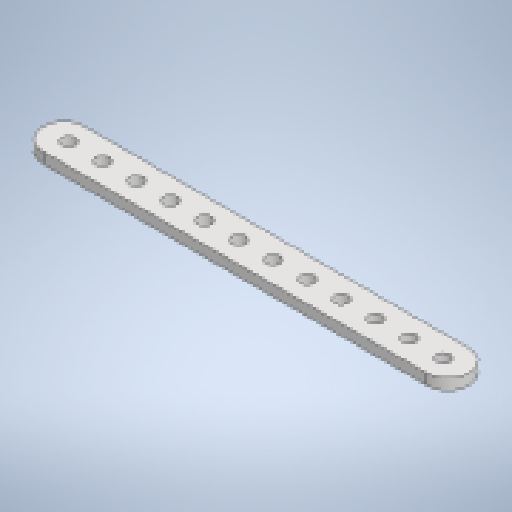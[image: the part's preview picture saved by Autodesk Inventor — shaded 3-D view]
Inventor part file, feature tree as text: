
AUTODESK INVENTOR PART (.ipt)
format: ipt  version: 2024.1 (Build 281209000, 209)  size: 283,648 bytes
history: native  units: mm
features: extrude x2, sketch x2, fillet x1
ambient origin geometry x8: Origin, YZ Plane, XZ Plane, XY Plane, X Axis, Y Axis, Z Axis, Center Point
bodies: Solid1 (feature_tree)
feature tree (5):
  extrude  "Extrusion1"  Depth=10.0mm
  extrude  "Extrusion2"  Depth=2.5mm TaperAngle=0.0deg
  fillet  "Fillet1"  Radius=6.0mm
  sketch  "Sketch1"  dims[d0=10.0mm d1=100.0mm]
  sketch  "Sketch2"  dims[d2=50.0mm d3=2.5mm d4=0.0mm d5=6.0mm d6=3.2mm d7=10.0mm d8=5.0mm d10=100.0mm d11=120.0mm d13=8.0mm d14=10.0mm d16=10.0mm d18=6.0mm d19=0.0mm d20=0.0mm d21=5.0mm]
